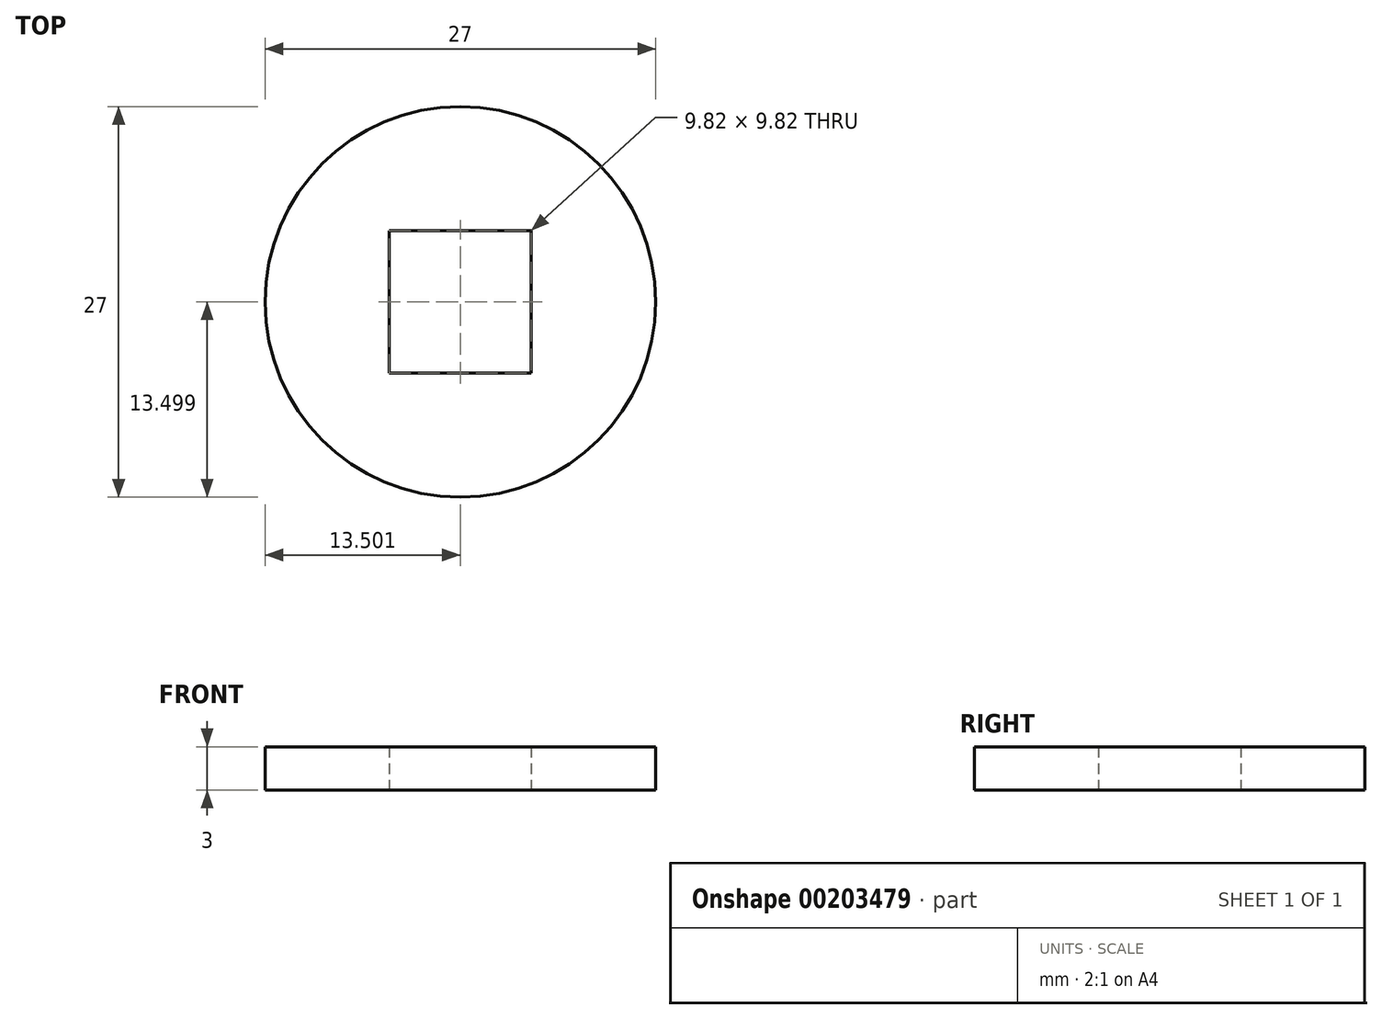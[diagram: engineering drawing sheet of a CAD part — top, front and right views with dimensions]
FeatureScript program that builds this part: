
annotation { "Feature Type Name" : "Feature", "Feature Type Description" : "" }
export const myFeature = defineFeature(function(context is Context, id is Id, definition is map)
    precondition{}
    {
        {
            var Q0;
            Q0=qCreatedBy(makeId("Top.planeOp"),FACE);
            var sketch = newSketch(context, id + "F0", { "sketchPlane" : qUnion([Q0])});
            skLineSegment(sketch, "E0", {"start": v(22.83, -6.92) * mm, "end": v(12.65, -17.1) * mm});
            skCircle(sketch, "E1", {"center": v(17.74, -12.01) * mm, "radius": 13.5 * mm});
            skLineSegment(sketch, "E2.0", {"start": v(12.83, -16.92) * mm, "end": v(22.65, -16.92) * mm});
            skLineSegment(sketch, "E2.1", {"start": v(12.83, -7.1) * mm, "end": v(12.83, -16.92) * mm});
            skLineSegment(sketch, "E2.2", {"start": v(12.83, -7.1) * mm, "end": v(22.65, -7.1) * mm});
            skLineSegment(sketch, "E2.3", {"start": v(22.65, -7.1) * mm, "end": v(22.65, -16.92) * mm});
            skSolve(sketch);
        }
        {
            var Q0;
            Q0 = qSketchRegion(id + "F0", true);
            extrude(context, id + "F1", {"entities" : qUnion([Q0]), "depth" : 3 * mm});
        }
    });
